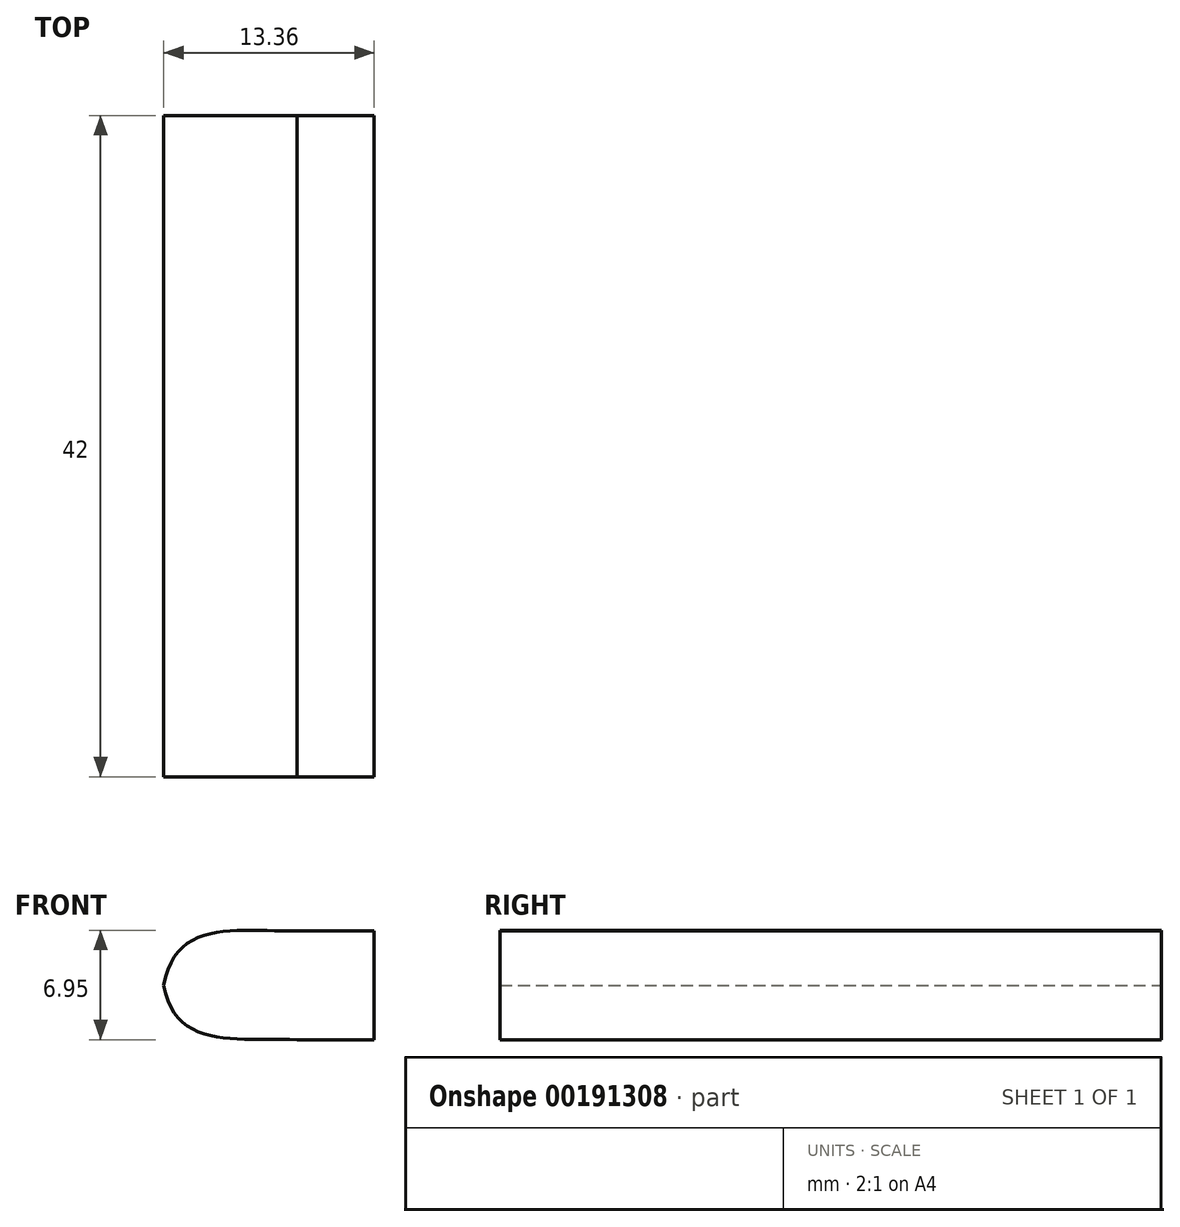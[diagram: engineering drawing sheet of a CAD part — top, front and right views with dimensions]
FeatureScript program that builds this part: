
annotation { "Feature Type Name" : "Feature", "Feature Type Description" : "" }
export const myFeature = defineFeature(function(context is Context, id is Id, definition is map)
    precondition{}
    {
        {
            var Q0;
            Q0=qCreatedBy(makeId("Front.planeOp"),FACE);
            var sketch = newSketch(context, id + "F0", { "sketchPlane" : qUnion([Q0])});
            skLineSegment(sketch, "E0", {"start": v(4.98, 3.76) * mm, "end": v(0.1, 3.76) * mm});
            skLineSegment(sketch, "E1", {"start": v(0.1, 3.76) * mm, "end": v(0.1, 0.3) * mm});
            skLineSegment(sketch, "E2", {"start": v(0.1, 0.3) * mm, "end": v(4.98, 0.3) * mm});
            skLineSegment(sketch, "E3", {"start": v(4.98, 0.3) * mm, "end": v(4.98, 3.76) * mm});
            skPoint(sketch, "E4", {"position": v(-8.38, 0.3) * mm});
            skFitSpline(sketch, "E5", {"points": [v(0.1, 3.76) * mm, v(-8.38, 0.3) * mm], "startDerivative": vector(-11, -0.16) * mm, "endDerivative": vector(-2.22, -12.96) * mm});
            skPoint(sketch, "E6", {"position": v(0.1, -3.14) * mm});
            skLineSegment(sketch, "E7", {"start": v(0.1, 0.3) * mm, "end": v(0.1, -3.14) * mm});
            skLineSegment(sketch, "E8", {"start": v(0.1, -3.14) * mm, "end": v(4.98, -3.14) * mm});
            skLineSegment(sketch, "E9", {"start": v(4.98, -3.14) * mm, "end": v(4.98, 0.3) * mm});
            skFitSpline(sketch, "E10", {"points": [v(0.1, -3.14) * mm, v(-8.38, 0.3) * mm], "startDerivative": vector(-11, 0.55) * mm, "endDerivative": vector(-2.22, 12.57) * mm});
            skSolve(sketch);
        }
        {
            var Q0;
            Q0=makeQuery(id+"F0.imprint","IMPRINT",FACE,{"disambiguationData":[TD([[makeQuery(id+"F0.imprint","IMPRINT",EDGE,{"derivedFrom":sQuery(id+"F0.wireOp",EDGE,"E1")}),-1.0]])]});
            var Q1;
            Q1=makeQuery(id+"F0.imprint","IMPRINT",FACE,{"disambiguationData":[TD([[makeQuery(id+"F0.imprint","IMPRINT",EDGE,{"derivedFrom":sQuery(id+"F0.wireOp",EDGE,"E2")}),-1.0]])]});
            var Q2;
            Q2=makeQuery(id+"F0.imprint","IMPRINT",FACE,{"disambiguationData":[TD([[makeQuery(id+"F0.imprint","IMPRINT",EDGE,{"derivedFrom":sQuery(id+"F0.wireOp",EDGE,"E0")}),1.0]])]});
            extrude(context, id + "F1", {"entities" : qUnion([Q0, Q1, Q2]), "depth" : 42 * mm});
        }
    });
